# Revit family: Deck_Drain-Promenade-Jay R.Smith-Square_Type-1425_Series
name_source: partatom
category: Plumbing Fixtures
units: mm (PartAtom-declared; Revit-internal decimal feet)

## family parameters
Always vertical = Yes
Cut with Voids When Loaded = No
OmniClass Number = 23.70.50.21.24
OmniClass Title = Waste Water Drains
Part Type = Normal
Room Calculation Point = No
Round Connector Dimension = Use Radius
Shared = No
Work Plane-Based = Yes

## types (5) — shared parameters
Adjustable Height = 4"
Adjustable Height Constraint = 4"
Assembly Code = D2030300
Body Material = Cast Iron-Jay R Smith-Duco Coated
C - Underdeck Clamp = No
CL - "L" Shaped Underdeck Clamp = No
CW Connection = No
Default Elevation = 0"
Description = 14in. Promenade Deck Drain
Diameter = 15 3/4"
E - Extension (specify height) = No
Expansion Joint (Specify Fig. 1710) = No
G - Galvanized Cast Iron = No
HP - Heel Proof Grate = No
HW Connection = No
Installation Type = Deck Mounted
L - Speedi-Set Service Weight - 02"(50), 03"(75) & 04"(100) sizes only = No
LXH - Speedi-Set Extra Heavy - 02"(50), 03"(75) & 04"(100) sizes only = No
Load Rating = Load between 2,000 lbs. (900 kg) and 4,999 lbs. (2,250 kg) per ASME A112.6.3 Floor Drain Standard.
M - Ducolite Iron Grate = No
Manufacturer = Jay R. Smith
Material = Cast Iron-Jay R Smith-Duco Coated
NB - Nickel Bronze Top = No
NO-HUB Adaptor = No
PB - Polished Bronze Top = No
Product Documentation Link = https://www.jrsmith.com
Product Page URL = https://www.jrsmith.com
R - Sump Receiver = No
RDP - Roof Deck Plate = No
U - Vandal Proof Grate = No
URL = http://www.jrsmith.com
Vent Connection = No
W - 3/8" (10) Dia. Holes - (8) Required = No
Waste Connection = Yes

## per-type parameters (varying)
| type | B Dimension | Connection Description | Outlet Diameter | Outlet Radius | Radius 1 | Thickness |
| 1425T02 | 5 3/4" | 2" Threaded Outlet Connection | 2" | 1" | 1 1/4" | 3" |
| 1425T03 | 6 1/4" | 3" Threaded Outlet Connection | 3" | 1 1/2" | 1 3/4" | 3" |
| 1425T04 | 6 3/4" | 4" Threaded Outlet Connection | 4" | 2" | 2 1/4" | 3" |
| 1425T05 | 7 1/4" | 5" Threaded Outlet Connection | 5" | 2 1/2" | 2 3/4" | 2 1/2" |
| 1425T06 | 7 3/4" | 6" Threaded Outlet Connection | 6" | 3" | 3 1/4" | 2" |

note: column(s) folded — value = type name in every type: Model

## geometry (parser evidence)
native form markers: Sweep x3
no freeform markers — native parametric forms only
